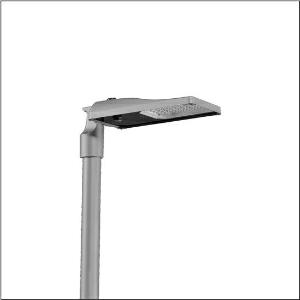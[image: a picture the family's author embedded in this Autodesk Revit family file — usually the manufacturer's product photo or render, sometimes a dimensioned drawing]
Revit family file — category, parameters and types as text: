
# Revit family: streetlight_sl_31_mini___st1_0a_5xh6d3at08ja_2b3a
name_source: partatom
category: Lighting Fixtures
units: mm (PartAtom-declared; Revit-internal decimal feet)

## family parameters
Cut with Voids When Loaded = No
Host = Face
Light Source = No
Part Type = Normal
Room Calculation Point = No
Round Connector Dimension = Use Diameter
Shared = No

## types (1)
- --- (1 x LED, 12270 lm, 82.5 W, 3000K)
    Apparent Load = 83 VA
    CIE Flux Codes = 40 73 97 100 100
    Color Rendering = 70
    Color Temperature = 3000K
    Default Elevation = 1800 mm
    Description = Streetlight SL 31 mini, mast luminaire, primary light control with lens, of PMMA, primary optical cover: cover, of toughened safety glass, transparent, light distribution: ST1.0a, light emission: direct distribution, primary light characteristic: asymmetric, installation type: post-top, side-entry, LED, High Power LED, rated luminous flux: 12.270lm, luminous efficacy: 149lm/W, light colour: 730, colour temperature: 3000K, control: presetting dimming logarithmic, flexible luminous flux parameterisation, time-dependent luminous flux control, constant luminous flux control, power reduction, intelligent temperature release in ECG and LED module, overheat protection, with cable H07RN-F 2x 1.5mm², mains connection: 220..240V, AC, 50/60Hz, connection cable pre-assembled, cable length: 10,5m, start of lifetime: 83W, end of service life: 90W, reduction: 37W, luminaire housing, of diecast aluminium, powder-coated, Siteco® metallic grey (DB 702S), corrosivity category C5 high according to DIN EN ISO 12944, sealing non-destructively replaceable, multi-level sealing system, mast flange (76/60mm) included as standard, inclination: -15°..+20° (post-top) | -20°..+20° (side-entry), adjustable in 5° steps, no sealing on luminaire upper side, Smart Interface below and above, protection rating (complete): IP66, insulation class (complete): insulation class II (safety insulation), certification: CE, ENEC, ENEC+, VDE, UKCA, ZD4i, impact resistance: IK09, permissible operating ambient temperature for outdoor applications: -40..+50°C, standard-compliant lighting for roads and squares, packaging unit: 1 piece

Light Distribution: ST1.0a
    Height = 76 mm
    Lamp = 1 x LED
    Lamp Light Flux = 12270 lm
    Lamp Power = 82.5 W
    Lamp count = 1
    Length = 547 mm
    Luminous efficacy = 149 lm/W
    Manufacturer = Siteco
    ModVariant = No
    Model = 5XH6D3AT08JA
    Number of Poles = 1
    OnlyDefault = Yes
    Power Factor = 1
    Product Name = Streetlight SL 31 mini | ST1.0a
    Product group = mast luminaire | pylon top
    ProductGroupID = 6100
    Protection Class = Protection class II
    Protection Degree = IP 66
    RLX_Detail_Level = 1
    RLX_Emergency_Light_Flux = 0 lm
    RLX_Emergency_Type = 0
    RLX_Emergency_Type_DB = No
    RlxData = <blob elided: 40169 chars, md5=4e8acc6b>
    Socket = socket
    Standby Power = 0 W
    System Light Flux = 12270 lm
    System Power = 83 W
    Type Comments = factory setting: luminous flux: 100 % | dim-lin: 254 | 870 mA
    Type Image = l_1300332.jpg
    URL = http://relux.com
    VarID = @adj_007775
    Voltage = 0 V
    Weight = 0.00 kg
    Width = 265 mm

## geometry (parser evidence)
native form markers: Blend x4, Sweep x10
no freeform markers — native parametric forms only
